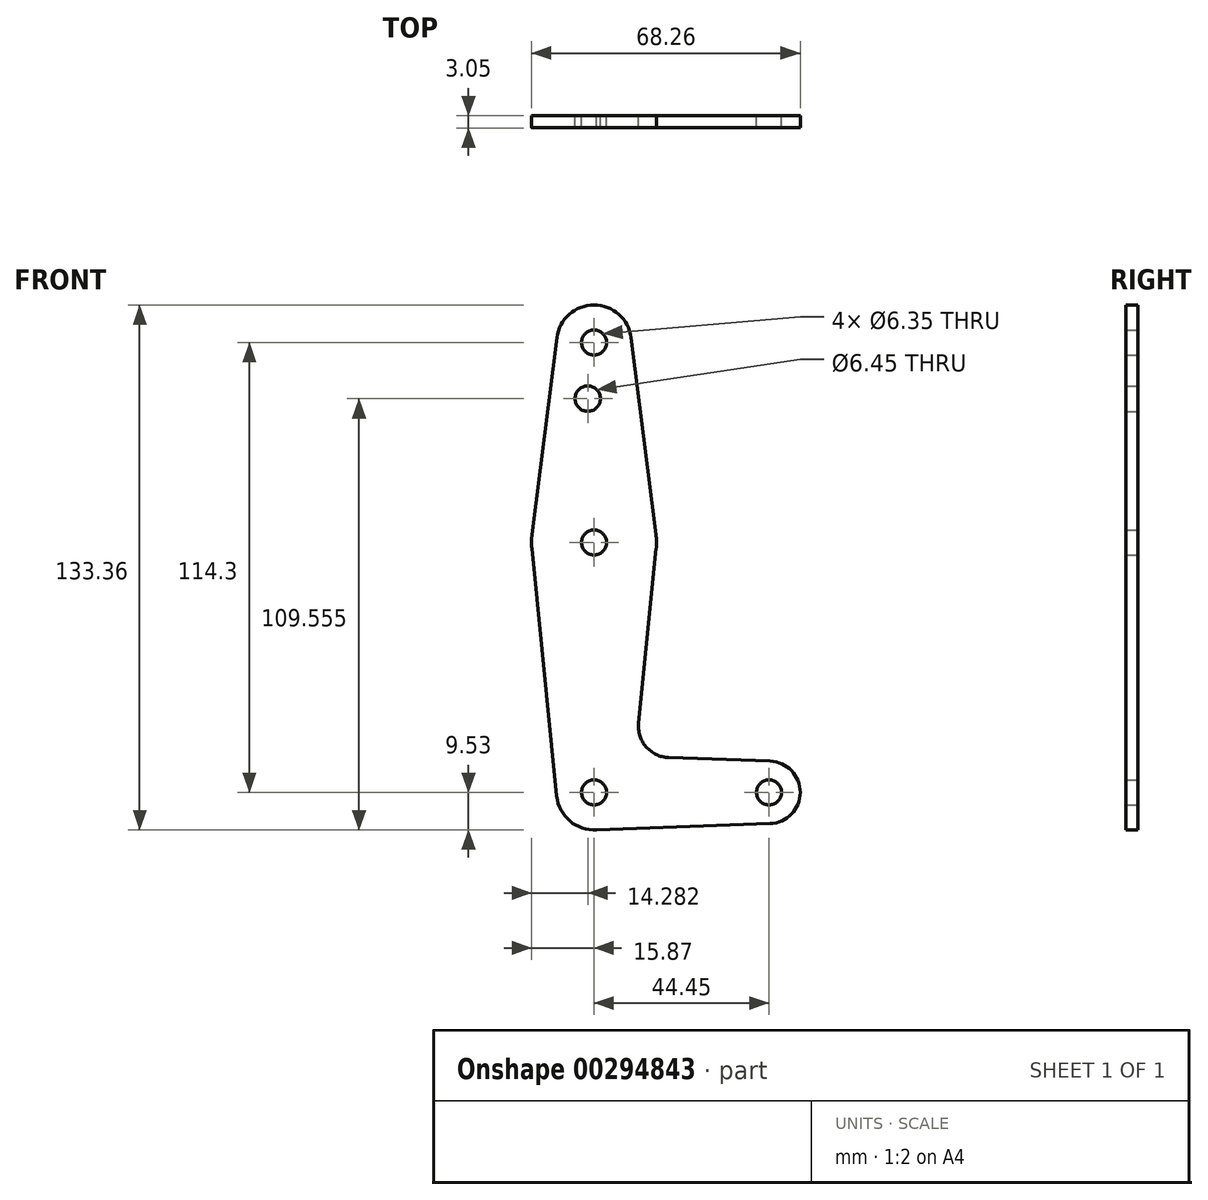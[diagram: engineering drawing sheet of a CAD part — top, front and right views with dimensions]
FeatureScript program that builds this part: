
annotation { "Feature Type Name" : "Feature", "Feature Type Description" : "" }
export const myFeature = defineFeature(function(context is Context, id is Id, definition is map)
    precondition{}
    {
        {
            var Q0;
            Q0=qCreatedBy(makeId("Front.planeOp"),FACE);
            var sketch = newSketch(context, id + "F0", { "sketchPlane" : qUnion([Q0])});
            skCircle(sketch, "E0", {"center": v(0, 0) * mm, "radius": 9.53 * mm});
            skCircle(sketch, "E1", {"center": v(0, 63.5) * mm, "radius": 15.88 * mm});
            skCircle(sketch, "E2", {"center": v(0, 114.3) * mm, "radius": 9.53 * mm});
            skCircle(sketch, "E3", {"center": v(44.45, 0) * mm, "radius": 7.94 * mm});
            skLineSegment(sketch, "E4", {"start": v(0, 114.3) * mm, "end": v(0, 63.5) * mm, "construction": true});
            skLineSegment(sketch, "E5", {"start": v(0, 63.5) * mm, "end": v(0, 0) * mm, "construction": true});
            skLineSegment(sketch, "E6", {"start": v(0, 0) * mm, "end": v(44.45, 0) * mm, "construction": true});
            skLineSegment(sketch, "E7", {"start": v(-9.45, 115.5) * mm, "end": v(-15.75, 65.48) * mm});
            skLineSegment(sketch, "E8", {"start": v(-15.8, 61.91) * mm, "end": v(-9.48, -0.95) * mm});
            skLineSegment(sketch, "E9", {"start": v(15.75, 65.48) * mm, "end": v(9.45, 115.5) * mm});
            skLineSegment(sketch, "E10", {"start": v(0, -9.52) * mm, "end": v(44.73, -7.93) * mm});
            skLineSegment(sketch, "E11", {"start": v(11.3, 17.6) * mm, "end": v(15.8, 61.9) * mm});
            skLineSegment(sketch, "E12", {"start": v(18.93, 8.85) * mm, "end": v(44.73, 7.93) * mm});
            skCircle(sketch, "E13", {"center": v(0, 114.3) * mm, "radius": 3.18 * mm});
            skCircle(sketch, "E14", {"center": v(-1.59, 100.03) * mm, "radius": 3.22 * mm});
            skCircle(sketch, "E15", {"center": v(0, 63.5) * mm, "radius": 3.18 * mm});
            skCircle(sketch, "E16", {"center": v(0, 0) * mm, "radius": 3.18 * mm});
            skCircle(sketch, "E17", {"center": v(44.45, 0) * mm, "radius": 3.18 * mm});
            skArc(sketch, "E18.filletArc", {"start": v(11.3, 17.6) * mm, "mid": v(13.22, 11.57) * mm, "end": v(18.93, 8.85) * mm});
            skSolve(sketch);
        }
        {
            var Q0;
            Q0 = qSketchRegion(id + "F0", true);
            extrude(context, id + "F1", {"entities" : qUnion([Q0]), "depth" : 3.05 * mm});
        }
    });
